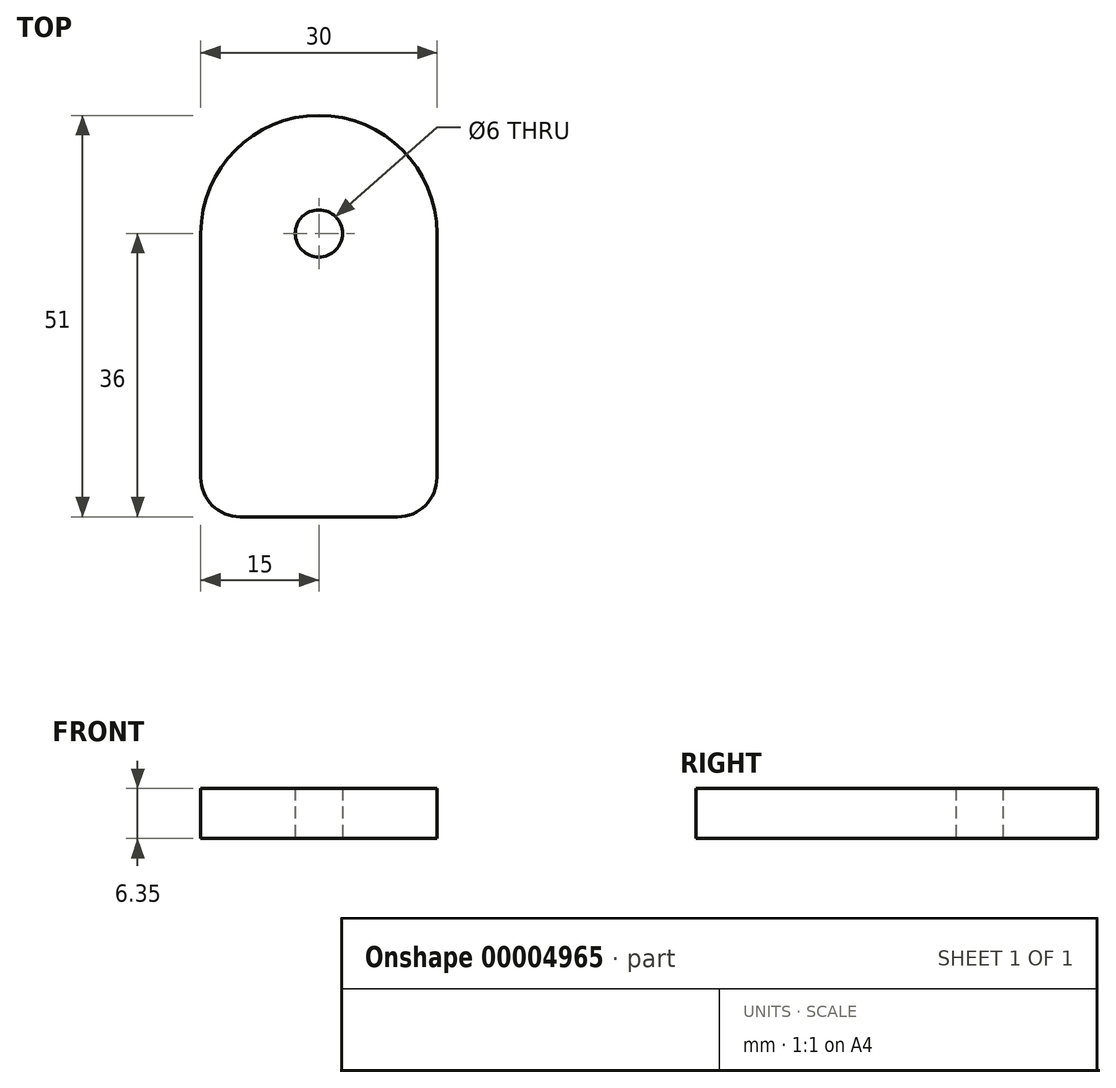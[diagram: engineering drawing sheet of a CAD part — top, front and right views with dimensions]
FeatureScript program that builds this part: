
annotation { "Feature Type Name" : "Feature", "Feature Type Description" : "" }
export const myFeature = defineFeature(function(context is Context, id is Id, definition is map)
    precondition{}
    {
        {
            var Q0;
            Q0=qCreatedBy(makeId("Top.planeOp"),FACE);
            var sketch = newSketch(context, id + "F0", { "sketchPlane" : qUnion([Q0])});
            skCircle(sketch, "E0", {"center": v(0, 0) * mm, "radius": 3 * mm});
            skArc(sketch, "E1", {"start": v(15, 0) * mm, "mid": v(0, 15) * mm, "end": v(-15, 0) * mm});
            skLineSegment(sketch, "E2", {"start": v(0, 0) * mm, "end": v(0, -20) * mm, "construction": true});
            skLineSegment(sketch, "E3", {"start": v(0, -20) * mm, "end": v(0, -116) * mm, "construction": true});
            skPoint(sketch, "E4", {"position": v(0, -31) * mm});
            skLineSegment(sketch, "E5", {"start": v(-15, 0) * mm, "end": v(-15, -36) * mm});
            skLineSegment(sketch, "E6", {"start": v(15, 0) * mm, "end": v(15, -36) * mm});
            skLineSegment(sketch, "E7", {"start": v(15, -36) * mm, "end": v(-15, -36) * mm});
            skSolve(sketch);
        }
        {
            var Q0;
            Q0 = qSketchRegion(id + "F0", true);
            extrude(context, id + "F1", {"entities" : qUnion([Q0]), "depth" : 6.35 * mm});
        }
        {
            var Q0;
            Q0=makeQuery(id+"F1.opExtrude","SWEPT_EDGE",EDGE,{"disambiguationData":[OSD([sQuery(id+"F0.wireOp",EDGE,"E5"),sQuery(id+"F0.wireOp",EDGE,"E7")])]});
            var Q1;
            Q1=makeQuery(id+"F1.opExtrude","SWEPT_EDGE",EDGE,{"disambiguationData":[OSD([sQuery(id+"F0.wireOp",EDGE,"E6"),sQuery(id+"F0.wireOp",EDGE,"E7")])]});
            fillet(context, id + "F2", {"entities" : qUnion([Q0, Q1]), "radius" : 5 * mm, "tangentPropagation" : true, "allowEdgeOverflow" : false});
        }
    });
